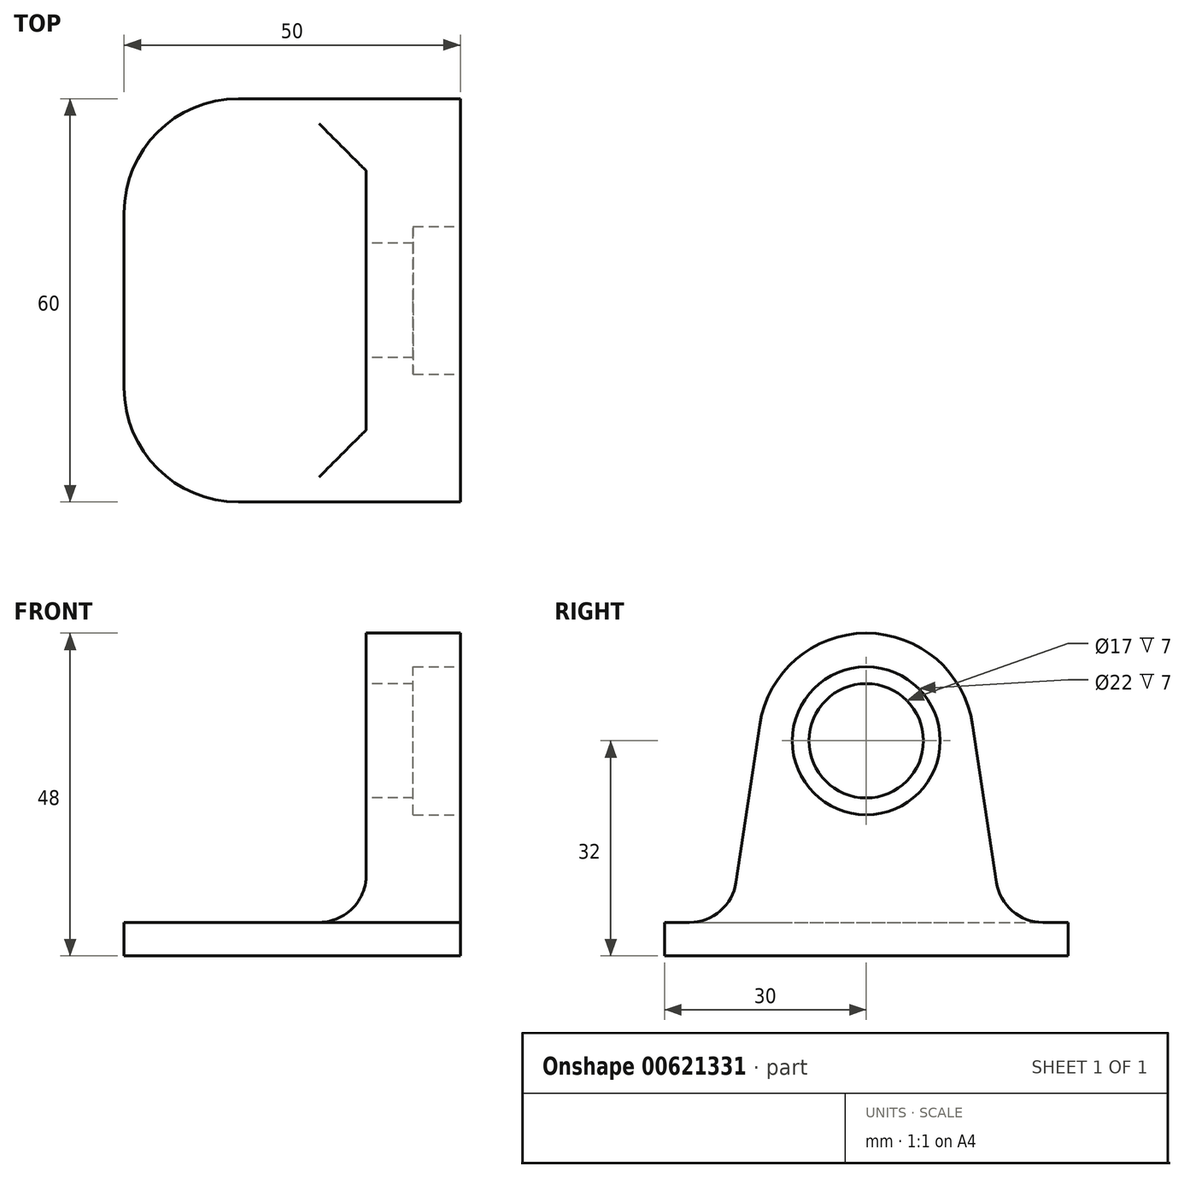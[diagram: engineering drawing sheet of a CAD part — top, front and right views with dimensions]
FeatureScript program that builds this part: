
annotation { "Feature Type Name" : "Feature", "Feature Type Description" : "" }
export const myFeature = defineFeature(function(context is Context, id is Id, definition is map)
    precondition{}
    {
        {
            var Q0;
            Q0=qCreatedBy(makeId("Right.planeOp"),FACE);
            var sketch = newSketch(context, id + "F0", { "sketchPlane" : qUnion([Q0])});
            skCircle(sketch, "E0", {"center": v(0, 0) * mm, "radius": 8.5 * mm});
            skArc(sketch, "E1", {"start": v(15.82, 2.38) * mm, "mid": v(0, 16) * mm, "end": v(-15.82, 2.38) * mm});
            skLineSegment(sketch, "E2", {"start": v(-15.82, 2.38) * mm, "end": v(-21, -32) * mm});
            skLineSegment(sketch, "E3", {"start": v(-21, -32) * mm, "end": v(21, -32) * mm});
            skLineSegment(sketch, "E4", {"start": v(21, -32) * mm, "end": v(15.82, 2.38) * mm});
            skLineSegment(sketch, "E5", {"start": v(0, 0) * mm, "end": v(0, -42.46) * mm, "construction": true});
            skPoint(sketch, "E5.endSnap0", {"position": v(0, -32) * mm});
            skSolve(sketch);
        }
        {
            var Q0;
            Q0 = qSketchRegion(id + "F0", true);
            extrude(context, id + "F1", {"entities" : qUnion([Q0]), "depth" : 14 * mm, "offsetDistance" : 25 * mm});
        }
        {
            var Q0;
            Q0=makeQuery(id+"F1.opExtrude","CAP_FACE",FACE,{"disambiguationData":[OSD([sQuery(id+"F0.wireOp",EDGE,"E0"),sQuery(id+"F0.wireOp",EDGE,"E1"),sQuery(id+"F0.wireOp",EDGE,"E2"),sQuery(id+"F0.wireOp",EDGE,"E3"),sQuery(id+"F0.wireOp",EDGE,"E4")])],"isStart":false});
            var sketch = newSketch(context, id + "F2", { "sketchPlane" : qUnion([Q0])});
            skCircle(sketch, "E6", {"center": v(0, 0) * mm, "radius": 11 * mm});
            skSolve(sketch);
        }
        {
            var Q0;
            Q0 = qSketchRegion(id + "F2", true);
            extrude(context, id + "F3", {"entities" : qUnion([Q0]), "operationType" : NewBodyOperationType.REMOVE, "oppositeDirection" : true, "depth" : 7 * mm, "offsetDistance" : 25 * mm});
        }
        {
            var Q0;
            Q0=makeQuery(id+"F1.opExtrude","SWEPT_FACE",FACE,{"disambiguationData":[OSD([sQuery(id+"F0.wireOp",EDGE,"E3")])]});
            var sketch = newSketch(context, id + "F4", { "sketchPlane" : qUnion([Q0])});
            skLineSegment(sketch, "E7.bottom", {"start": v(14, 30) * mm, "end": v(-36, 30) * mm});
            skLineSegment(sketch, "E7.top", {"start": v(14, -30) * mm, "end": v(-36, -30) * mm});
            skLineSegment(sketch, "E7.left", {"start": v(14, 30) * mm, "end": v(14, -30) * mm});
            skLineSegment(sketch, "E7.right", {"start": v(-36, 30) * mm, "end": v(-36, -30) * mm});
            skSolve(sketch);
        }
        {
            var Q0;
            Q0 = qSketchRegion(id + "F4", true);
            extrude(context, id + "F5", {"entities" : qUnion([Q0]), "operationType" : NewBodyOperationType.ADD, "oppositeDirection" : true, "depth" : 5 * mm, "offsetDistance" : 25 * mm});
        }
        {
            var Q0;
            Q0=makeQuery(id+"F5.boolean.opBoolean","INTERSECT",EDGE,{"derivedFrom":[makeQuery(id+"F1.opExtrude","SWEPT_FACE",FACE,{"disambiguationData":[OSD([sQuery(id+"F0.wireOp",EDGE,"E2")])]}),makeQuery(id+"F5.opExtrude","CAP_FACE",FACE,{"disambiguationData":[OSD([sQuery(id+"F4.wireOp",EDGE,"E7.bottom"),sQuery(id+"F4.wireOp",EDGE,"E7.top"),sQuery(id+"F4.wireOp",EDGE,"E7.left"),sQuery(id+"F4.wireOp",EDGE,"E7.right")])],"isStart":false})]});
            var Q1;
            Q1=makeQuery(id+"F5.boolean.opBoolean","INTERSECT",EDGE,{"derivedFrom":[makeQuery(id+"F1.opExtrude","CAP_FACE",FACE,{"disambiguationData":[OSD([sQuery(id+"F0.wireOp",EDGE,"E0"),sQuery(id+"F0.wireOp",EDGE,"E1"),sQuery(id+"F0.wireOp",EDGE,"E2"),sQuery(id+"F0.wireOp",EDGE,"E3"),sQuery(id+"F0.wireOp",EDGE,"E4")])],"isStart":true}),makeQuery(id+"F5.opExtrude","CAP_FACE",FACE,{"disambiguationData":[OSD([sQuery(id+"F4.wireOp",EDGE,"E7.bottom"),sQuery(id+"F4.wireOp",EDGE,"E7.top"),sQuery(id+"F4.wireOp",EDGE,"E7.left"),sQuery(id+"F4.wireOp",EDGE,"E7.right")])],"isStart":false})]});
            var Q2;
            Q2=makeQuery(id+"F5.boolean.opBoolean","INTERSECT",EDGE,{"derivedFrom":[makeQuery(id+"F1.opExtrude","SWEPT_FACE",FACE,{"disambiguationData":[OSD([sQuery(id+"F0.wireOp",EDGE,"E4")])]}),makeQuery(id+"F5.opExtrude","CAP_FACE",FACE,{"disambiguationData":[OSD([sQuery(id+"F4.wireOp",EDGE,"E7.bottom"),sQuery(id+"F4.wireOp",EDGE,"E7.top"),sQuery(id+"F4.wireOp",EDGE,"E7.left"),sQuery(id+"F4.wireOp",EDGE,"E7.right")])],"isStart":false})]});
            fillet(context, id + "F6", {"entities" : qUnion([Q0, Q1, Q2]), "radius" : 7 * mm, "tangentPropagation" : true, "allowEdgeOverflow" : false});
        }
        {
            var Q0;
            Q0=makeQuery(id+"F5.opExtrude","SWEPT_EDGE",EDGE,{"disambiguationData":[OSD([sQuery(id+"F4.wireOp",EDGE,"E7.bottom"),sQuery(id+"F4.wireOp",EDGE,"E7.right")])]});
            var Q1;
            Q1=makeQuery(id+"F5.opExtrude","SWEPT_EDGE",EDGE,{"disambiguationData":[OSD([sQuery(id+"F4.wireOp",EDGE,"E7.top"),sQuery(id+"F4.wireOp",EDGE,"E7.right")])]});
            fillet(context, id + "F7", {"entities" : qUnion([Q0, Q1]), "radius" : 17 * mm, "tangentPropagation" : true, "allowEdgeOverflow" : false});
        }
    });
